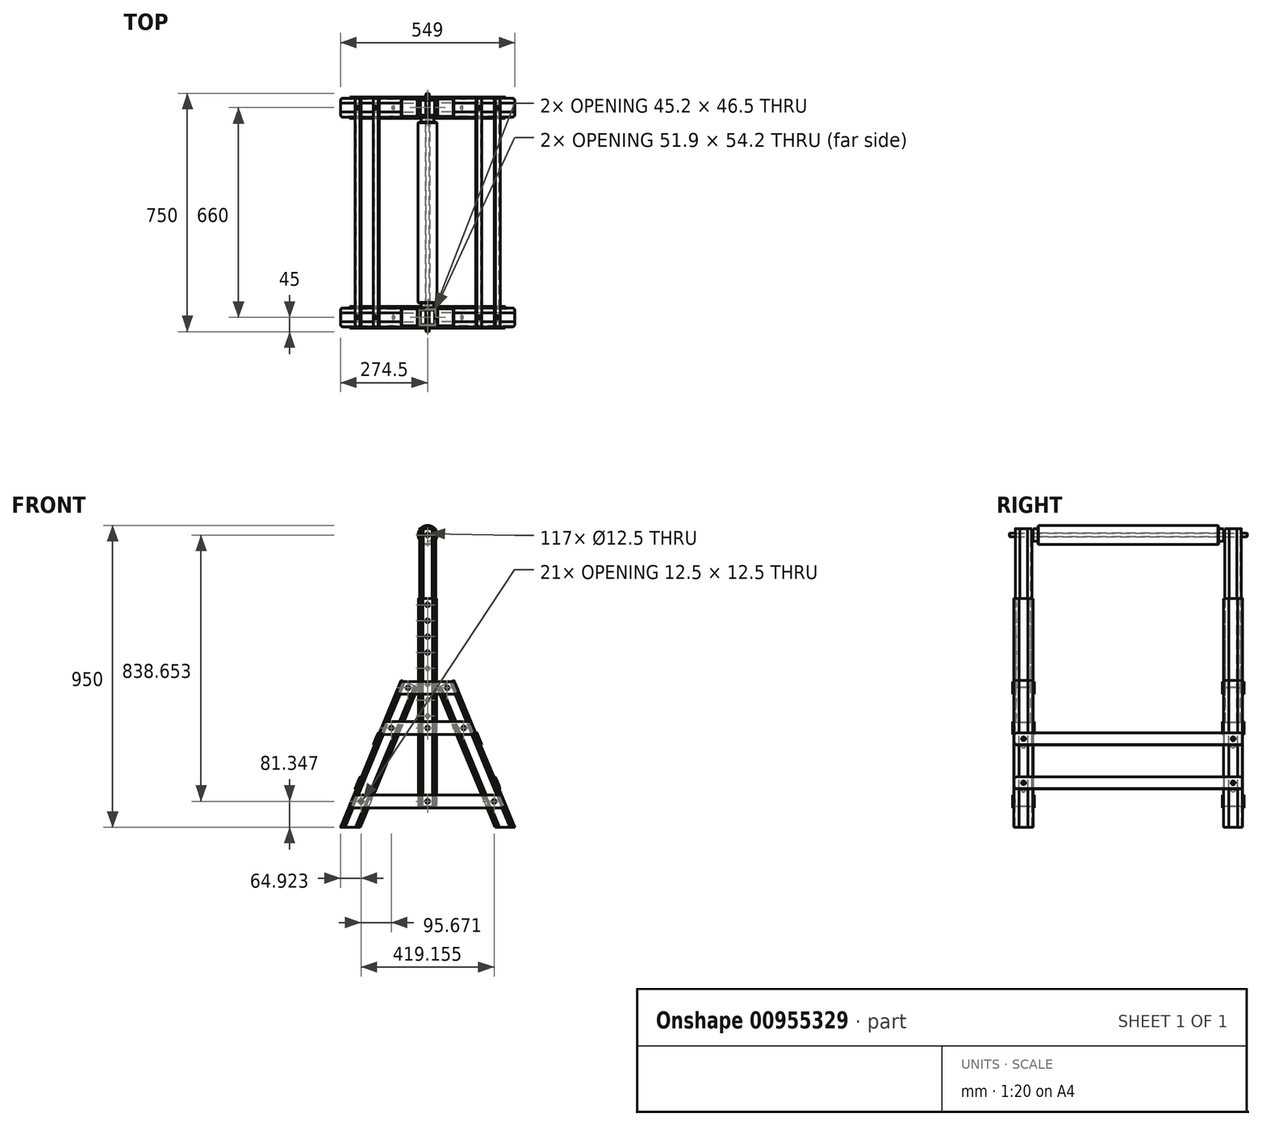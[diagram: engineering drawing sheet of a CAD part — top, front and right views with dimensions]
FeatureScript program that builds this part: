
annotation { "Feature Type Name" : "Feature", "Feature Type Description" : "" }
export const myFeature = defineFeature(function(context is Context, id is Id, definition is map)
    precondition{}
    {
        {
            var Q0;
            Q0=qCreatedBy(makeId("Front.planeOp"),FACE);
            var sketch = newSketch(context, id + "F0", { "sketchPlane" : qUnion([Q0])});
            skLineSegment(sketch, "E0", {"start": v(0, 0) * mm, "end": v(-62.45, 0) * mm});
            skLineSegment(sketch, "E1", {"start": v(-62.45, 0) * mm, "end": v(-244.65, 439.86) * mm});
            skLineSegment(sketch, "E2", {"start": v(-244.65, 439.86) * mm, "end": v(-191.34, 461.94) * mm});
            skLineSegment(sketch, "E3", {"start": v(-191.34, 461.94) * mm, "end": v(0, 0) * mm});
            skLineSegment(sketch, "E4", {"start": v(-218, 450.9) * mm, "end": v(-31.23, 0) * mm, "construction": true});
            skCircle(sketch, "E5", {"center": v(-213.02, 438.89) * mm, "radius": 6.25 * mm});
            skCircle(sketch, "E6", {"center": v(-64.92, 81.35) * mm, "radius": 6.25 * mm});
            skCircle(sketch, "E7", {"center": v(-160.6, 312.32) * mm, "radius": 6.25 * mm});
            skSolve(sketch);
        }
        {
            var Q0;
            Q0=qSketchRegion(id+"F0",true);
            extrude(context, id + "F1", {"entities" : qUnion([Q0]), "depth" : 60 * mm, "offsetDistance" : 25 * mm});
        }
        {
            var Q0;
            Q0=makeQuery(id+"F1.opExtrude","SWEPT_FACE",FACE,{"disambiguationData":[OSD([sQuery(id+"F0.wireOp",EDGE,"E3")])]});
            var sketch = newSketch(context, id + "F2", { "sketchPlane" : qUnion([Q0])});
            skLineSegment(sketch, "E8", {"start": v(-30, 500) * mm, "end": v(-30, 0) * mm, "construction": true});
            skCircle(sketch, "E9", {"center": v(-30, 150) * mm, "radius": 6.25 * mm});
            skCircle(sketch, "E10", {"center": v(-30, 300) * mm, "radius": 6.25 * mm});
            skSolve(sketch);
        }
        {
            var Q0;
            Q0=qSketchRegion(id+"F2",true);
            var Q1;
            Q1=makeQuery(id+"F1.opExtrude","SWEPT_FACE",FACE,{"disambiguationData":[OSD([sQuery(id+"F0.wireOp",EDGE,"E1")])]});
            extrude(context, id + "F3", {"entities" : qUnion([Q0]), "operationType" : NewBodyOperationType.REMOVE, "endBound" : BoundingType.UP_TO_SURFACE, "oppositeDirection" : true, "depth" : 25 * mm, "endBoundEntityFace" : qUnion([Q1]), "offsetDistance" : 25 * mm});
        }
        {
            var Q0;
            Q0=makeQuery(id+"F1.opExtrude","CAP_EDGE",EDGE,{"disambiguationData":[OSD([sQuery(id+"F0.wireOp",EDGE,"E1")])],"isStart":false});
            var Q1;
            Q1=makeQuery(id+"F1.opExtrude","CAP_EDGE",EDGE,{"disambiguationData":[OSD([sQuery(id+"F0.wireOp",EDGE,"E3")])],"isStart":false});
            var Q2;
            Q2=makeQuery(id+"F1.opExtrude","CAP_EDGE",EDGE,{"disambiguationData":[OSD([sQuery(id+"F0.wireOp",EDGE,"E1")])],"isStart":true});
            var Q3;
            Q3=makeQuery(id+"F1.opExtrude","CAP_EDGE",EDGE,{"disambiguationData":[OSD([sQuery(id+"F0.wireOp",EDGE,"E3")])],"isStart":true});
            fillet(context, id + "F4", {"entities" : qUnion([Q0, Q1, Q2, Q3]), "radius" : 7.5 * mm, "tangentPropagation" : true, "allowEdgeOverflow" : false});
        }
        {
            var Q0;
            Q0=makeQuery(id+"F1.opExtrude","SWEPT_FACE",FACE,{"disambiguationData":[OSD([sQuery(id+"F0.wireOp",EDGE,"E2")])]});
            var sketch = newSketch(context, id + "F5", { "sketchPlane" : qUnion([Q0])});
            skLineSegment(sketch, "E11", {"start": v(-57.7, -30) * mm, "end": v(-28.85, -30) * mm, "construction": true});
            skLineSegment(sketch, "E12", {"start": v(-28.85, -30) * mm, "end": v(-28.85, -60) * mm, "construction": true});
            skArc(sketch, "E13.0", {"start": v(-54.8, -52.5) * mm, "mid": v(-53.45, -55.75) * mm, "end": v(-50.2, -57.1) * mm});
            skLineSegment(sketch, "E14", {"start": v(-57.4, -30) * mm, "end": v(-57.4, -44) * mm});
            skLineSegment(sketch, "E15", {"start": v(-57.4, -44) * mm, "end": v(-57.7, -44) * mm});
            skLineSegment(sketch, "E16", {"start": v(-50.2, -60) * mm, "end": v(-49.2, -59) * mm});
            skLineSegment(sketch, "E17", {"start": v(-49.2, -59) * mm, "end": v(-48.2, -60) * mm});
            skLineSegment(sketch, "E18", {"start": v(-48.2, -60) * mm, "end": v(-47.2, -59) * mm});
            skLineSegment(sketch, "E19", {"start": v(-47.2, -59) * mm, "end": v(-46.2, -60) * mm});
            skLineSegment(sketch, "E20", {"start": v(-46.2, -60) * mm, "end": v(-45.2, -59) * mm});
            skLineSegment(sketch, "E21", {"start": v(-45.2, -59) * mm, "end": v(-44.2, -60) * mm});
            skLineSegment(sketch, "E22", {"start": v(-50.2, -57.1) * mm, "end": v(-28.85, -57.1) * mm});
            skLineSegment(sketch, "E23", {"start": v(-54.8, -52.5) * mm, "end": v(-54.8, -30) * mm});
            skLineSegment(sketch, "E24.MirrorCS", {"start": v(-0.3, -44) * mm, "end": v(0, -44) * mm});
            skLineSegment(sketch, "E25.MirrorCS", {"start": v(-12.5, -59) * mm, "end": v(-13.5, -60) * mm});
            skLineSegment(sketch, "E26.MirrorCS", {"start": v(-7.5, -60) * mm, "end": v(-8.5, -59) * mm});
            skLineSegment(sketch, "E27.MirrorCS", {"start": v(-8.5, -59) * mm, "end": v(-9.5, -60) * mm});
            skLineSegment(sketch, "E28.MirrorCS", {"start": v(-11.5, -60) * mm, "end": v(-12.5, -59) * mm});
            skLineSegment(sketch, "E29.MirrorCS", {"start": v(-10.5, -59) * mm, "end": v(-11.5, -60) * mm});
            skLineSegment(sketch, "E30.MirrorCS", {"start": v(-9.5, -60) * mm, "end": v(-10.5, -59) * mm});
            skLineSegment(sketch, "E31.MirrorCS", {"start": v(-0.3, -30) * mm, "end": v(-0.3, -44) * mm});
            skLineSegment(sketch, "E32.MirrorCS", {"start": v(-7.5, -57.1) * mm, "end": v(-28.85, -57.1) * mm});
            skLineSegment(sketch, "E33.MirrorCS", {"start": v(-2.9, -52.5) * mm, "end": v(-2.9, -30) * mm});
            skArc(sketch, "E34.MirrorCS", {"start": v(-2.9, -52.5) * mm, "mid": v(-4.25, -55.75) * mm, "end": v(-7.5, -57.1) * mm});
            skLineSegment(sketch, "E35.MirrorCS", {"start": v(-57.4, -16) * mm, "end": v(-57.7, -16) * mm});
            skLineSegment(sketch, "E36.MirrorCS", {"start": v(-50.2, 0) * mm, "end": v(-49.2, -1) * mm});
            skLineSegment(sketch, "E37.MirrorCS", {"start": v(-45.2, -1) * mm, "end": v(-44.2, 0) * mm});
            skLineSegment(sketch, "E38.MirrorCS", {"start": v(-47.2, -1) * mm, "end": v(-46.2, 0) * mm});
            skLineSegment(sketch, "E39.MirrorCS", {"start": v(-48.2, 0) * mm, "end": v(-47.2, -1) * mm});
            skLineSegment(sketch, "E40.MirrorCS", {"start": v(-49.2, -1) * mm, "end": v(-48.2, 0) * mm});
            skLineSegment(sketch, "E41.MirrorCS", {"start": v(-46.2, 0) * mm, "end": v(-45.2, -1) * mm});
            skLineSegment(sketch, "E42.MirrorCS", {"start": v(-57.4, -30) * mm, "end": v(-57.4, -16) * mm});
            skArc(sketch, "E43.MirrorCS", {"start": v(-54.8, -7.5) * mm, "mid": v(-53.45, -4.25) * mm, "end": v(-50.2, -2.9) * mm});
            skLineSegment(sketch, "E44.MirrorCS", {"start": v(-50.2, -2.9) * mm, "end": v(-28.85, -2.9) * mm});
            skLineSegment(sketch, "E45.MirrorCS", {"start": v(-54.8, -7.5) * mm, "end": v(-54.8, -30) * mm});
            skLineSegment(sketch, "E46.MirrorCS", {"start": v(-0.3, -16) * mm, "end": v(0, -16) * mm});
            skLineSegment(sketch, "E47.MirrorCS", {"start": v(-8.5, -1) * mm, "end": v(-9.5, 0) * mm});
            skLineSegment(sketch, "E48.MirrorCS", {"start": v(-11.5, 0) * mm, "end": v(-12.5, -1) * mm});
            skLineSegment(sketch, "E49.MirrorCS", {"start": v(-10.5, -1) * mm, "end": v(-11.5, 0) * mm});
            skLineSegment(sketch, "E50.MirrorCS", {"start": v(-9.5, 0) * mm, "end": v(-10.5, -1) * mm});
            skLineSegment(sketch, "E51.MirrorCS", {"start": v(-12.5, -1) * mm, "end": v(-13.5, 0) * mm});
            skLineSegment(sketch, "E52.MirrorCS", {"start": v(-7.5, 0) * mm, "end": v(-8.5, -1) * mm});
            skLineSegment(sketch, "E53.MirrorCS", {"start": v(-0.3, -30) * mm, "end": v(-0.3, -16) * mm});
            skLineSegment(sketch, "E54.MirrorCS", {"start": v(-2.9, -7.5) * mm, "end": v(-2.9, -30) * mm});
            skArc(sketch, "E55.MirrorCS", {"start": v(-2.9, -7.5) * mm, "mid": v(-4.25, -4.25) * mm, "end": v(-7.5, -2.9) * mm});
            skLineSegment(sketch, "E56.MirrorCS", {"start": v(-7.5, -2.9) * mm, "end": v(-28.85, -2.9) * mm});
            skSolve(sketch);
        }
        {
            var Q0;
            {var subQ0=sQuery(id+"F5.wireOp",EDGE,"E20");Q0=makeQuery(id+"F5.imprint","IMPRINT",FACE,{"disambiguationData":[TD([[makeQuery(id+"F5.imprint","IMPRINT",EDGE,{"derivedFrom":subQ0}),-1.0]])]});}
            var Q1;
            {var subQ0=sQuery(id+"F5.wireOp",EDGE,"E18");Q1=makeQuery(id+"F5.imprint","IMPRINT",FACE,{"disambiguationData":[TD([[makeQuery(id+"F5.imprint","IMPRINT",EDGE,{"derivedFrom":subQ0}),-1.0]])]});}
            var Q2;
            {var subQ0=sQuery(id+"F5.wireOp",EDGE,"E16");Q2=makeQuery(id+"F5.imprint","IMPRINT",FACE,{"disambiguationData":[TD([[makeQuery(id+"F5.imprint","IMPRINT",EDGE,{"derivedFrom":subQ0}),-1.0]])]});}
            var Q3;
            {var subQ0=sQuery(id+"F5.wireOp",EDGE,"E26.MirrorCS");Q3=makeQuery(id+"F5.imprint","IMPRINT",FACE,{"disambiguationData":[TD([[makeQuery(id+"F5.imprint","IMPRINT",EDGE,{"derivedFrom":subQ0}),1.0]])]});}
            var Q4;
            {var subQ0=sQuery(id+"F5.wireOp",EDGE,"E29.MirrorCS");Q4=makeQuery(id+"F5.imprint","IMPRINT",FACE,{"disambiguationData":[TD([[makeQuery(id+"F5.imprint","IMPRINT",EDGE,{"derivedFrom":subQ0}),1.0]])]});}
            var Q5;
            {var subQ0=sQuery(id+"F5.wireOp",EDGE,"E25.MirrorCS");Q5=makeQuery(id+"F5.imprint","IMPRINT",FACE,{"disambiguationData":[TD([[makeQuery(id+"F5.imprint","IMPRINT",EDGE,{"derivedFrom":subQ0}),1.0]])]});}
            var Q6;
            {var subQ1=sQuery(id+"F5.wireOp",EDGE,"E24.MirrorCS");Q6=makeQuery(id+"F5.imprint","IMPRINT",FACE,{"disambiguationData":[TD([[makeQuery(id+"F5.imprint","IMPRINT",EDGE,{"derivedFrom":subQ1}),1.0]])]});}
            var Q7;
            Q7=makeQuery(id+"F5.imprint","IMPRINT",FACE,{"disambiguationData":[TD([[makeQuery(id+"F5.imprint","IMPRINT",EDGE,{"derivedFrom":sQuery(id+"F5.wireOp",EDGE,"E14")}),-1.0]])]});
            var Q8;
            {var subQ0=sQuery(id+"F5.wireOp",EDGE,"E36.MirrorCS");Q8=makeQuery(id+"F5.imprint","IMPRINT",FACE,{"disambiguationData":[TD([[makeQuery(id+"F5.imprint","IMPRINT",EDGE,{"derivedFrom":subQ0}),1.0]])]});}
            var Q9;
            {var subQ0=sQuery(id+"F5.wireOp",EDGE,"E38.MirrorCS");Q9=makeQuery(id+"F5.imprint","IMPRINT",FACE,{"disambiguationData":[TD([[makeQuery(id+"F5.imprint","IMPRINT",EDGE,{"derivedFrom":subQ0}),1.0]])]});}
            var Q10;
            {var subQ0=sQuery(id+"F5.wireOp",EDGE,"E37.MirrorCS");Q10=makeQuery(id+"F5.imprint","IMPRINT",FACE,{"disambiguationData":[TD([[makeQuery(id+"F5.imprint","IMPRINT",EDGE,{"derivedFrom":subQ0}),1.0]])]});}
            var Q11;
            {var subQ0=sQuery(id+"F5.wireOp",EDGE,"E47.MirrorCS");Q11=makeQuery(id+"F5.imprint","IMPRINT",FACE,{"disambiguationData":[TD([[makeQuery(id+"F5.imprint","IMPRINT",EDGE,{"derivedFrom":subQ0}),-1.0]])]});}
            var Q12;
            {var subQ0=sQuery(id+"F5.wireOp",EDGE,"E49.MirrorCS");Q12=makeQuery(id+"F5.imprint","IMPRINT",FACE,{"disambiguationData":[TD([[makeQuery(id+"F5.imprint","IMPRINT",EDGE,{"derivedFrom":subQ0}),-1.0]])]});}
            var Q13;
            {var subQ0=sQuery(id+"F5.wireOp",EDGE,"E48.MirrorCS");Q13=makeQuery(id+"F5.imprint","IMPRINT",FACE,{"disambiguationData":[TD([[makeQuery(id+"F5.imprint","IMPRINT",EDGE,{"derivedFrom":subQ0}),-1.0]])]});}
            var Q14;
            Q14=makeQuery(id+"F5.imprint","IMPRINT",FACE,{"disambiguationData":[TD([[makeQuery(id+"F5.imprint","IMPRINT",EDGE,{"derivedFrom":sQuery(id+"F5.wireOp",EDGE,"E13.0")}),1.0]])]});
            var Q15;
            Q15=makeQuery(id+"F1.opExtrude","SWEPT_FACE",FACE,{"disambiguationData":[OSD([sQuery(id+"F0.wireOp",EDGE,"E0")])]});
            extrude(context, id + "F6", {"entities" : qUnion([Q0, Q1, Q2, Q3, Q4, Q5, Q6, Q7, Q8, Q9, Q10, Q11, Q12, Q13, Q14]), "operationType" : NewBodyOperationType.REMOVE, "endBound" : BoundingType.UP_TO_SURFACE, "oppositeDirection" : true, "depth" : 25 * mm, "endBoundEntityFace" : qUnion([Q15]), "offsetDistance" : 25 * mm});
        }
        {
            var Q0;
            Q0=makeQuery(id+"F1.opExtrude","CAP_FACE",FACE,{"disambiguationData":[OSD([sQuery(id+"F0.wireOp",EDGE,"E0"),sQuery(id+"F0.wireOp",EDGE,"E1"),sQuery(id+"F0.wireOp",EDGE,"E2"),sQuery(id+"F0.wireOp",EDGE,"E3"),sQuery(id+"F0.wireOp",EDGE,"E5"),sQuery(id+"F0.wireOp",EDGE,"E6")])],"isStart":false});
            var sketch = newSketch(context, id + "F7", { "sketchPlane" : qUnion([Q0])});
            skLineSegment(sketch, "E57", {"start": v(-245.65, 720) * mm, "end": v(-245.65, 66.35) * mm});
            skLineSegment(sketch, "E58", {"start": v(-245.65, 66.35) * mm, "end": v(-303.35, 66.35) * mm});
            skLineSegment(sketch, "E59", {"start": v(-303.35, 66.35) * mm, "end": v(-303.35, 720) * mm});
            skLineSegment(sketch, "E60", {"start": v(-303.35, 720) * mm, "end": v(-245.65, 720) * mm});
            skLineSegment(sketch, "E61", {"start": v(-303.35, 75.1) * mm, "end": v(24.53, 75.1) * mm, "construction": true});
            skLineSegment(sketch, "E62", {"start": v(-274.5, 720) * mm, "end": v(-274.5, 66.35) * mm, "construction": true});
            skCircle(sketch, "E63", {"center": v(-274.5, 81.35) * mm, "radius": 6.25 * mm});
            skLineSegment(sketch, "E64", {"start": v(-303.35, 306.07) * mm, "end": v(155.56, 306.07) * mm, "construction": true});
            skCircle(sketch, "E65", {"center": v(-274.5, 312.32) * mm, "radius": 6.25 * mm});
            skCircle(sketch, "E66", {"center": v(-274.5, 650) * mm, "radius": 6.25 * mm});
            skCircle(sketch, "E67", {"center": v(-274.5, 600) * mm, "radius": 6.25 * mm});
            skCircle(sketch, "E68", {"center": v(-274.5, 700) * mm, "radius": 6.25 * mm});
            skCircle(sketch, "E69", {"center": v(-274.5, 550) * mm, "radius": 6.25 * mm});
            skSolve(sketch);
        }
        {
            var Q0;
            Q0=qSketchRegion(id+"F7",true);
            extrude(context, id + "F8", {"entities" : qUnion([Q0]), "oppositeDirection" : true, "depth" : 60 * mm, "offsetDistance" : 25 * mm});
        }
        {
            var Q0;
            Q0=makeQuery(id+"F8.opExtrude","CAP_EDGE",EDGE,{"disambiguationData":[OSD([sQuery(id+"F7.wireOp",EDGE,"E59")])],"isStart":false});
            var Q1;
            Q1=makeQuery(id+"F8.opExtrude","CAP_EDGE",EDGE,{"disambiguationData":[OSD([sQuery(id+"F7.wireOp",EDGE,"E59")])],"isStart":true});
            var Q2;
            Q2=makeQuery(id+"F8.opExtrude","CAP_EDGE",EDGE,{"disambiguationData":[OSD([sQuery(id+"F7.wireOp",EDGE,"E57")])],"isStart":true});
            var Q3;
            Q3=makeQuery(id+"F8.opExtrude","CAP_EDGE",EDGE,{"disambiguationData":[OSD([sQuery(id+"F7.wireOp",EDGE,"E57")])],"isStart":false});
            fillet(context, id + "F9", {"entities" : qUnion([Q0, Q1, Q2, Q3]), "radius" : 7.5 * mm, "tangentPropagation" : true, "allowEdgeOverflow" : false});
        }
        {
            var Q0;
            Q0=makeQuery(id+"F8.opExtrude","SWEPT_FACE",FACE,{"disambiguationData":[OSD([sQuery(id+"F7.wireOp",EDGE,"E60")])]});
            var sketch = newSketch(context, id + "F10", { "sketchPlane" : qUnion([Q0])});
            skLineSegment(sketch, "E70", {"start": v(-274.5, -60) * mm, "end": v(-274.5, -30) * mm, "construction": true});
            skPoint(sketch, "E70.endSnap0", {"position": v(-303.35, -30) * mm});
            skLineSegment(sketch, "E71", {"start": v(-274.5, -30) * mm, "end": v(-303.35, -30) * mm, "construction": true});
            skLineSegment(sketch, "E72", {"start": v(-295.85, -60) * mm, "end": v(-294.85, -59) * mm});
            skLineSegment(sketch, "E73", {"start": v(-294.85, -59) * mm, "end": v(-293.85, -60) * mm});
            skLineSegment(sketch, "E74", {"start": v(-293.85, -60) * mm, "end": v(-292.85, -59) * mm});
            skLineSegment(sketch, "E75", {"start": v(-292.85, -59) * mm, "end": v(-291.85, -60) * mm});
            skLineSegment(sketch, "E76", {"start": v(-291.85, -60) * mm, "end": v(-290.85, -59) * mm});
            skLineSegment(sketch, "E77", {"start": v(-290.85, -59) * mm, "end": v(-289.85, -60) * mm});
            skLineSegment(sketch, "E78", {"start": v(-303.05, -30) * mm, "end": v(-303.05, -44) * mm});
            skLineSegment(sketch, "E79", {"start": v(-303.05, -44) * mm, "end": v(-303.35, -44) * mm});
            skArc(sketch, "E80.0", {"start": v(-300.45, -52.5) * mm, "mid": v(-299.1, -55.75) * mm, "end": v(-295.85, -57.1) * mm});
            skLineSegment(sketch, "E81", {"start": v(-295.85, -57.1) * mm, "end": v(-274.5, -57.1) * mm});
            skLineSegment(sketch, "E82", {"start": v(-300.45, -52.5) * mm, "end": v(-300.45, -30) * mm});
            skLineSegment(sketch, "E83.MirrorCS", {"start": v(-255.15, -60) * mm, "end": v(-256.15, -59) * mm});
            skLineSegment(sketch, "E84.MirrorCS", {"start": v(-245.95, -44) * mm, "end": v(-245.65, -44) * mm});
            skLineSegment(sketch, "E85.MirrorCS", {"start": v(-254.15, -59) * mm, "end": v(-255.15, -60) * mm});
            skLineSegment(sketch, "E86.MirrorCS", {"start": v(-256.15, -59) * mm, "end": v(-257.15, -60) * mm});
            skLineSegment(sketch, "E87.MirrorCS", {"start": v(-257.15, -60) * mm, "end": v(-258.15, -59) * mm});
            skLineSegment(sketch, "E88.MirrorCS", {"start": v(-253.15, -60) * mm, "end": v(-254.15, -59) * mm});
            skLineSegment(sketch, "E89.MirrorCS", {"start": v(-258.15, -59) * mm, "end": v(-259.15, -60) * mm});
            skLineSegment(sketch, "E90.MirrorCS", {"start": v(-248.55, -52.5) * mm, "end": v(-248.55, -30) * mm});
            skLineSegment(sketch, "E91.MirrorCS", {"start": v(-245.95, -30) * mm, "end": v(-245.95, -44) * mm});
            skLineSegment(sketch, "E92.MirrorCS", {"start": v(-253.15, -57.1) * mm, "end": v(-274.5, -57.1) * mm});
            skArc(sketch, "E93.MirrorCS", {"start": v(-248.55, -52.5) * mm, "mid": v(-249.9, -55.75) * mm, "end": v(-253.15, -57.1) * mm});
            skLineSegment(sketch, "E94.MirrorCS", {"start": v(-290.85, -1) * mm, "end": v(-289.85, 0) * mm});
            skLineSegment(sketch, "E95.MirrorCS", {"start": v(-303.05, -16) * mm, "end": v(-303.35, -16) * mm});
            skLineSegment(sketch, "E96.MirrorCS", {"start": v(-295.85, 0) * mm, "end": v(-294.85, -1) * mm});
            skLineSegment(sketch, "E97.MirrorCS", {"start": v(-293.85, 0) * mm, "end": v(-292.85, -1) * mm});
            skLineSegment(sketch, "E98.MirrorCS", {"start": v(-294.85, -1) * mm, "end": v(-293.85, 0) * mm});
            skLineSegment(sketch, "E99.MirrorCS", {"start": v(-291.85, 0) * mm, "end": v(-290.85, -1) * mm});
            skLineSegment(sketch, "E100.MirrorCS", {"start": v(-292.85, -1) * mm, "end": v(-291.85, 0) * mm});
            skLineSegment(sketch, "E101.MirrorCS", {"start": v(-300.45, -7.5) * mm, "end": v(-300.45, -30) * mm});
            skLineSegment(sketch, "E102.MirrorCS", {"start": v(-295.85, -2.9) * mm, "end": v(-274.5, -2.9) * mm});
            skArc(sketch, "E103.MirrorCS", {"start": v(-300.45, -7.5) * mm, "mid": v(-299.1, -4.25) * mm, "end": v(-295.85, -2.9) * mm});
            skLineSegment(sketch, "E104.MirrorCS", {"start": v(-303.05, -30) * mm, "end": v(-303.05, -16) * mm});
            skLineSegment(sketch, "E105.MirrorCS", {"start": v(-253.15, 0) * mm, "end": v(-254.15, -1) * mm});
            skLineSegment(sketch, "E106.MirrorCS", {"start": v(-258.15, -1) * mm, "end": v(-259.15, 0) * mm});
            skLineSegment(sketch, "E107.MirrorCS", {"start": v(-255.15, 0) * mm, "end": v(-256.15, -1) * mm});
            skLineSegment(sketch, "E108.MirrorCS", {"start": v(-257.15, 0) * mm, "end": v(-258.15, -1) * mm});
            skLineSegment(sketch, "E109.MirrorCS", {"start": v(-256.15, -1) * mm, "end": v(-257.15, 0) * mm});
            skLineSegment(sketch, "E110.MirrorCS", {"start": v(-245.95, -16) * mm, "end": v(-245.65, -16) * mm});
            skLineSegment(sketch, "E111.MirrorCS", {"start": v(-254.15, -1) * mm, "end": v(-255.15, 0) * mm});
            skLineSegment(sketch, "E112.MirrorCS", {"start": v(-248.55, -7.5) * mm, "end": v(-248.55, -30) * mm});
            skLineSegment(sketch, "E113.MirrorCS", {"start": v(-245.95, -30) * mm, "end": v(-245.95, -16) * mm});
            skArc(sketch, "E114.MirrorCS", {"start": v(-248.55, -7.5) * mm, "mid": v(-249.9, -4.25) * mm, "end": v(-253.15, -2.9) * mm});
            skLineSegment(sketch, "E115.MirrorCS", {"start": v(-253.15, -2.9) * mm, "end": v(-274.5, -2.9) * mm});
            skSolve(sketch);
        }
        {
            var Q0;
            {var subQ0=sQuery(id+"F10.wireOp",EDGE,"E76");Q0=makeQuery(id+"F10.imprint","IMPRINT",FACE,{"disambiguationData":[TD([[makeQuery(id+"F10.imprint","IMPRINT",EDGE,{"derivedFrom":subQ0}),-1.0]])]});}
            var Q1;
            {var subQ0=sQuery(id+"F10.wireOp",EDGE,"E74");Q1=makeQuery(id+"F10.imprint","IMPRINT",FACE,{"disambiguationData":[TD([[makeQuery(id+"F10.imprint","IMPRINT",EDGE,{"derivedFrom":subQ0}),-1.0]])]});}
            var Q2;
            {var subQ0=sQuery(id+"F10.wireOp",EDGE,"E72");Q2=makeQuery(id+"F10.imprint","IMPRINT",FACE,{"disambiguationData":[TD([[makeQuery(id+"F10.imprint","IMPRINT",EDGE,{"derivedFrom":subQ0}),-1.0]])]});}
            var Q3;
            Q3=makeQuery(id+"F10.imprint","IMPRINT",FACE,{"disambiguationData":[TD([[makeQuery(id+"F10.imprint","IMPRINT",EDGE,{"derivedFrom":sQuery(id+"F10.wireOp",EDGE,"E78")}),-1.0]])]});
            var Q4;
            {var subQ0=sQuery(id+"F10.wireOp",EDGE,"E85.MirrorCS");Q4=makeQuery(id+"F10.imprint","IMPRINT",FACE,{"disambiguationData":[TD([[makeQuery(id+"F10.imprint","IMPRINT",EDGE,{"derivedFrom":subQ0}),1.0]])]});}
            var Q5;
            {var subQ0=sQuery(id+"F10.wireOp",EDGE,"E83.MirrorCS");Q5=makeQuery(id+"F10.imprint","IMPRINT",FACE,{"disambiguationData":[TD([[makeQuery(id+"F10.imprint","IMPRINT",EDGE,{"derivedFrom":subQ0}),1.0]])]});}
            var Q6;
            {var subQ0=sQuery(id+"F10.wireOp",EDGE,"E87.MirrorCS");Q6=makeQuery(id+"F10.imprint","IMPRINT",FACE,{"disambiguationData":[TD([[makeQuery(id+"F10.imprint","IMPRINT",EDGE,{"derivedFrom":subQ0}),1.0]])]});}
            var Q7;
            {var subQ1=sQuery(id+"F10.wireOp",EDGE,"E84.MirrorCS");Q7=makeQuery(id+"F10.imprint","IMPRINT",FACE,{"disambiguationData":[TD([[makeQuery(id+"F10.imprint","IMPRINT",EDGE,{"derivedFrom":subQ1}),1.0]])]});}
            var Q8;
            {var subQ0=sQuery(id+"F10.wireOp",EDGE,"E105.MirrorCS");Q8=makeQuery(id+"F10.imprint","IMPRINT",FACE,{"disambiguationData":[TD([[makeQuery(id+"F10.imprint","IMPRINT",EDGE,{"derivedFrom":subQ0}),-1.0]])]});}
            var Q9;
            {var subQ0=sQuery(id+"F10.wireOp",EDGE,"E107.MirrorCS");Q9=makeQuery(id+"F10.imprint","IMPRINT",FACE,{"disambiguationData":[TD([[makeQuery(id+"F10.imprint","IMPRINT",EDGE,{"derivedFrom":subQ0}),-1.0]])]});}
            var Q10;
            {var subQ0=sQuery(id+"F10.wireOp",EDGE,"E106.MirrorCS");Q10=makeQuery(id+"F10.imprint","IMPRINT",FACE,{"disambiguationData":[TD([[makeQuery(id+"F10.imprint","IMPRINT",EDGE,{"derivedFrom":subQ0}),-1.0]])]});}
            var Q11;
            {var subQ0=sQuery(id+"F10.wireOp",EDGE,"E96.MirrorCS");Q11=makeQuery(id+"F10.imprint","IMPRINT",FACE,{"disambiguationData":[TD([[makeQuery(id+"F10.imprint","IMPRINT",EDGE,{"derivedFrom":subQ0}),1.0]])]});}
            var Q12;
            {var subQ0=sQuery(id+"F10.wireOp",EDGE,"E97.MirrorCS");Q12=makeQuery(id+"F10.imprint","IMPRINT",FACE,{"disambiguationData":[TD([[makeQuery(id+"F10.imprint","IMPRINT",EDGE,{"derivedFrom":subQ0}),1.0]])]});}
            var Q13;
            {var subQ0=sQuery(id+"F10.wireOp",EDGE,"E94.MirrorCS");Q13=makeQuery(id+"F10.imprint","IMPRINT",FACE,{"disambiguationData":[TD([[makeQuery(id+"F10.imprint","IMPRINT",EDGE,{"derivedFrom":subQ0}),1.0]])]});}
            var Q14;
            Q14=makeQuery(id+"F10.imprint","IMPRINT",FACE,{"disambiguationData":[TD([[makeQuery(id+"F10.imprint","IMPRINT",EDGE,{"derivedFrom":sQuery(id+"F10.wireOp",EDGE,"E80.0")}),1.0]])]});
            var Q15;
            Q15=makeQuery(id+"F8.opExtrude","SWEPT_FACE",FACE,{"disambiguationData":[OSD([sQuery(id+"F7.wireOp",EDGE,"E58")])]});
            extrude(context, id + "F11", {"entities" : qUnion([Q0, Q1, Q2, Q3, Q4, Q5, Q6, Q7, Q8, Q9, Q10, Q11, Q12, Q13, Q14]), "operationType" : NewBodyOperationType.REMOVE, "endBound" : BoundingType.UP_TO_SURFACE, "oppositeDirection" : true, "depth" : 25 * mm, "endBoundEntityFace" : qUnion([Q15]), "offsetDistance" : 25 * mm});
        }
        {
            var Q0;
            Q0=makeQuery(id+"F11.boolean.opBoolean","COPY",FACE,{"derivedFrom":makeQuery(id+"F11.opExtrude","SWEPT_FACE",FACE,{"disambiguationData":[OSD([sQuery(id+"F10.wireOp",EDGE,"E82"),sQuery(id+"F10.wireOp",EDGE,"E101.MirrorCS")])]})});
            var Q1;
            Q1=makeQuery(id+"F11.boolean.opBoolean","COPY",FACE,{"derivedFrom":makeQuery(id+"F11.opExtrude","SWEPT_FACE",FACE,{"disambiguationData":[OSD([sQuery(id+"F10.wireOp",EDGE,"E90.MirrorCS"),sQuery(id+"F10.wireOp",EDGE,"E112.MirrorCS")])]})});
            cPlane(context, id + "F12", {"entities" : qUnion([Q0, Q1]), "cplaneType" : CPlaneType.MID_PLANE, "offset" : 25 * mm, "width" : 150 * mm, "height" : 150 * mm});
        }
        {
            var Q0;
            Q0=makeQuery(id+"F11.boolean.opBoolean","COPY",FACE,{"derivedFrom":makeQuery(id+"F11.opExtrude","SWEPT_FACE",FACE,{"disambiguationData":[OSD([sQuery(id+"F10.wireOp",EDGE,"E81"),sQuery(id+"F10.wireOp",EDGE,"E92.MirrorCS")])]})});
            var Q1;
            Q1=makeQuery(id+"F11.boolean.opBoolean","COPY",FACE,{"derivedFrom":makeQuery(id+"F11.opExtrude","SWEPT_FACE",FACE,{"disambiguationData":[OSD([sQuery(id+"F10.wireOp",EDGE,"E102.MirrorCS"),sQuery(id+"F10.wireOp",EDGE,"E115.MirrorCS")])]})});
            cPlane(context, id + "F13", {"entities" : qUnion([Q0, Q1]), "cplaneType" : CPlaneType.MID_PLANE, "offset" : 25 * mm, "width" : 150 * mm, "height" : 150 * mm});
        }
        {
            var Q0;
            Q0=makeQuery(id+"F8.opExtrude","CAP_EDGE",EDGE,{"disambiguationData":[OSD([sQuery(id+"F7.wireOp",EDGE,"E65")])],"isStart":false});
            cPlane(context, id + "F14", {"entities" : qUnion([Q0]), "cplaneType" : CPlaneType.LINE_ANGLE, "offset" : 25 * mm, "angle" : 0 * degree, "width" : 150 * mm, "height" : 150 * mm});
        }
        {
            var Q0;
            Q0=qCreatedBy(id+"F13.planeOp",FACE);
            var sketch = newSketch(context, id + "F15", { "sketchPlane" : qUnion([Q0])});
            skLineSegment(sketch, "E116", {"start": v(249, 940) * mm, "end": v(249, 330) * mm});
            skLineSegment(sketch, "E117", {"start": v(249, 330) * mm, "end": v(300, 330) * mm});
            skLineSegment(sketch, "E118", {"start": v(300, 330) * mm, "end": v(300, 940) * mm});
            skLineSegment(sketch, "E119", {"start": v(300, 940) * mm, "end": v(249, 940) * mm});
            skLineSegment(sketch, "E120", {"start": v(274.5, 940) * mm, "end": v(274.5, 330) * mm, "construction": true});
            skCircle(sketch, "E121", {"center": v(274.5, 550) * mm, "radius": 6.25 * mm});
            skCircle(sketch, "E122", {"center": v(274.5, 500) * mm, "radius": 6.25 * mm});
            skCircle(sketch, "E123", {"center": v(274.5, 650) * mm, "radius": 6.25 * mm});
            skCircle(sketch, "E124", {"center": v(274.5, 450) * mm, "radius": 6.25 * mm});
            skCircle(sketch, "E125", {"center": v(274.5, 700) * mm, "radius": 6.25 * mm});
            skCircle(sketch, "E126", {"center": v(274.5, 600) * mm, "radius": 6.25 * mm});
            skCircle(sketch, "E127", {"center": v(274.5, 400) * mm, "radius": 6.25 * mm});
            skCircle(sketch, "E128", {"center": v(274.5, 350) * mm, "radius": 6.25 * mm});
            skCircle(sketch, "E129", {"center": v(274.5, 920) * mm, "radius": 6.25 * mm});
            skSolve(sketch);
        }
        {
            var Q0;
            Q0=qSketchRegion(id+"F15",true);
            extrude(context, id + "F16", {"entities" : qUnion([Q0]), "endBound" : BoundingType.SYMMETRIC, "depth" : 52.3 * mm, "offsetDistance" : 25 * mm});
        }
        {
            var Q0;
            Q0=makeQuery(id+"F16.opExtrude","CAP_EDGE",EDGE,{"disambiguationData":[OSD([sQuery(id+"F15.wireOp",EDGE,"E116")])],"isStart":true});
            var Q1;
            Q1=makeQuery(id+"F16.opExtrude","CAP_EDGE",EDGE,{"disambiguationData":[OSD([sQuery(id+"F15.wireOp",EDGE,"E118")])],"isStart":true});
            var Q2;
            Q2=makeQuery(id+"F16.opExtrude","CAP_EDGE",EDGE,{"disambiguationData":[OSD([sQuery(id+"F15.wireOp",EDGE,"E116")])],"isStart":false});
            var Q3;
            Q3=makeQuery(id+"F16.opExtrude","CAP_EDGE",EDGE,{"disambiguationData":[OSD([sQuery(id+"F15.wireOp",EDGE,"E118")])],"isStart":false});
            fillet(context, id + "F17", {"entities" : qUnion([Q0, Q1, Q2, Q3]), "radius" : 7.5 * mm, "tangentPropagation" : true, "allowEdgeOverflow" : false});
        }
        {
            var Q0;
            Q0=makeQuery(id+"F16.opExtrude","SWEPT_FACE",FACE,{"disambiguationData":[OSD([sQuery(id+"F15.wireOp",EDGE,"E119")])]});
            var sketch = newSketch(context, id + "F18", { "sketchPlane" : qUnion([Q0])});
            skLineSegment(sketch, "E130", {"start": v(-249, -30) * mm, "end": v(-274.5, -30) * mm, "construction": true});
            skPoint(sketch, "E130.endSnap0", {"position": v(-274.5, -3.85) * mm});
            skLineSegment(sketch, "E131", {"start": v(-274.5, -30) * mm, "end": v(-274.5, -3.85) * mm, "construction": true});
            skLineSegment(sketch, "E132", {"start": v(-256.5, -3.85) * mm, "end": v(-257.5, -4.85) * mm});
            skLineSegment(sketch, "E133", {"start": v(-257.5, -4.85) * mm, "end": v(-258.5, -3.85) * mm});
            skLineSegment(sketch, "E134", {"start": v(-258.5, -3.85) * mm, "end": v(-259.5, -4.85) * mm});
            skLineSegment(sketch, "E135", {"start": v(-259.5, -4.85) * mm, "end": v(-260.5, -3.85) * mm});
            skLineSegment(sketch, "E136", {"start": v(-249.25, -30) * mm, "end": v(-249.25, -17.85) * mm});
            skLineSegment(sketch, "E137", {"start": v(-249.25, -17.85) * mm, "end": v(-249, -17.85) * mm});
            skArc(sketch, "E138.0", {"start": v(-251.9, -11.35) * mm, "mid": v(-253.25, -8.1) * mm, "end": v(-256.5, -6.75) * mm});
            skLineSegment(sketch, "E139", {"start": v(-256.5, -6.75) * mm, "end": v(-274.5, -6.75) * mm});
            skLineSegment(sketch, "E140", {"start": v(-251.9, -11.35) * mm, "end": v(-251.9, -30) * mm});
            skLineSegment(sketch, "E141.MirrorCS", {"start": v(-299.75, -17.85) * mm, "end": v(-300, -17.85) * mm});
            skLineSegment(sketch, "E142.MirrorCS", {"start": v(-292.5, -3.85) * mm, "end": v(-291.5, -4.85) * mm});
            skLineSegment(sketch, "E143.MirrorCS", {"start": v(-290.5, -3.85) * mm, "end": v(-289.5, -4.85) * mm});
            skLineSegment(sketch, "E144.MirrorCS", {"start": v(-289.5, -4.85) * mm, "end": v(-288.5, -3.85) * mm});
            skLineSegment(sketch, "E145.MirrorCS", {"start": v(-291.5, -4.85) * mm, "end": v(-290.5, -3.85) * mm});
            skLineSegment(sketch, "E146.MirrorCS", {"start": v(-299.75, -30) * mm, "end": v(-299.75, -17.85) * mm});
            skLineSegment(sketch, "E147.MirrorCS", {"start": v(-297.1, -11.35) * mm, "end": v(-297.1, -30) * mm});
            skLineSegment(sketch, "E148.MirrorCS", {"start": v(-292.5, -6.75) * mm, "end": v(-274.5, -6.75) * mm});
            skArc(sketch, "E149.MirrorCS", {"start": v(-297.1, -11.35) * mm, "mid": v(-295.75, -8.1) * mm, "end": v(-292.5, -6.75) * mm});
            skLineSegment(sketch, "E150.MirrorCS", {"start": v(-258.5, -56.15) * mm, "end": v(-259.5, -55.15) * mm});
            skLineSegment(sketch, "E151.MirrorCS", {"start": v(-249.25, -42.15) * mm, "end": v(-249, -42.15) * mm});
            skLineSegment(sketch, "E152.MirrorCS", {"start": v(-257.5, -55.15) * mm, "end": v(-258.5, -56.15) * mm});
            skLineSegment(sketch, "E153.MirrorCS", {"start": v(-256.5, -56.15) * mm, "end": v(-257.5, -55.15) * mm});
            skLineSegment(sketch, "E154.MirrorCS", {"start": v(-259.5, -55.15) * mm, "end": v(-260.5, -56.15) * mm});
            skLineSegment(sketch, "E155.MirrorCS", {"start": v(-256.5, -53.25) * mm, "end": v(-274.5, -53.25) * mm});
            skArc(sketch, "E156.MirrorCS", {"start": v(-251.9, -48.65) * mm, "mid": v(-253.25, -51.9) * mm, "end": v(-256.5, -53.25) * mm});
            skLineSegment(sketch, "E157.MirrorCS", {"start": v(-249.25, -30) * mm, "end": v(-249.25, -42.15) * mm});
            skLineSegment(sketch, "E158.MirrorCS", {"start": v(-251.9, -48.65) * mm, "end": v(-251.9, -30) * mm});
            skLineSegment(sketch, "E159.MirrorCS", {"start": v(-299.75, -42.15) * mm, "end": v(-300, -42.15) * mm});
            skLineSegment(sketch, "E160.MirrorCS", {"start": v(-291.5, -55.15) * mm, "end": v(-290.5, -56.15) * mm});
            skLineSegment(sketch, "E161.MirrorCS", {"start": v(-290.5, -56.15) * mm, "end": v(-289.5, -55.15) * mm});
            skLineSegment(sketch, "E162.MirrorCS", {"start": v(-292.5, -56.15) * mm, "end": v(-291.5, -55.15) * mm});
            skLineSegment(sketch, "E163.MirrorCS", {"start": v(-289.5, -55.15) * mm, "end": v(-288.5, -56.15) * mm});
            skLineSegment(sketch, "E164.MirrorCS", {"start": v(-299.75, -30) * mm, "end": v(-299.75, -42.15) * mm});
            skArc(sketch, "E165.MirrorCS", {"start": v(-297.1, -48.65) * mm, "mid": v(-295.75, -51.9) * mm, "end": v(-292.5, -53.25) * mm});
            skLineSegment(sketch, "E166.MirrorCS", {"start": v(-297.1, -48.65) * mm, "end": v(-297.1, -30) * mm});
            skLineSegment(sketch, "E167.MirrorCS", {"start": v(-292.5, -53.25) * mm, "end": v(-274.5, -53.25) * mm});
            skSolve(sketch);
        }
        {
            var Q0;
            Q0=makeQuery(id+"F18.imprint","IMPRINT",FACE,{"disambiguationData":[TD([[makeQuery(id+"F18.imprint","IMPRINT",EDGE,{"derivedFrom":sQuery(id+"F18.wireOp",EDGE,"E136")}),-1.0]])]});
            var Q1;
            {var subQ1=sQuery(id+"F18.wireOp",EDGE,"E141.MirrorCS");Q1=makeQuery(id+"F18.imprint","IMPRINT",FACE,{"disambiguationData":[TD([[makeQuery(id+"F18.imprint","IMPRINT",EDGE,{"derivedFrom":subQ1}),1.0]])]});}
            var Q2;
            {var subQ0=sQuery(id+"F18.wireOp",EDGE,"E160.MirrorCS");Q2=makeQuery(id+"F18.imprint","IMPRINT",FACE,{"disambiguationData":[TD([[makeQuery(id+"F18.imprint","IMPRINT",EDGE,{"derivedFrom":subQ0}),-1.0]])]});}
            var Q3;
            {var subQ0=sQuery(id+"F18.wireOp",EDGE,"E161.MirrorCS");Q3=makeQuery(id+"F18.imprint","IMPRINT",FACE,{"disambiguationData":[TD([[makeQuery(id+"F18.imprint","IMPRINT",EDGE,{"derivedFrom":subQ0}),-1.0]])]});}
            var Q4;
            {var subQ0=sQuery(id+"F18.wireOp",EDGE,"E152.MirrorCS");Q4=makeQuery(id+"F18.imprint","IMPRINT",FACE,{"disambiguationData":[TD([[makeQuery(id+"F18.imprint","IMPRINT",EDGE,{"derivedFrom":subQ0}),1.0]])]});}
            var Q5;
            {var subQ0=sQuery(id+"F18.wireOp",EDGE,"E150.MirrorCS");Q5=makeQuery(id+"F18.imprint","IMPRINT",FACE,{"disambiguationData":[TD([[makeQuery(id+"F18.imprint","IMPRINT",EDGE,{"derivedFrom":subQ0}),1.0]])]});}
            var Q6;
            {var subQ0=sQuery(id+"F18.wireOp",EDGE,"E132");Q6=makeQuery(id+"F18.imprint","IMPRINT",FACE,{"disambiguationData":[TD([[makeQuery(id+"F18.imprint","IMPRINT",EDGE,{"derivedFrom":subQ0}),-1.0]])]});}
            var Q7;
            {var subQ0=sQuery(id+"F18.wireOp",EDGE,"E134");Q7=makeQuery(id+"F18.imprint","IMPRINT",FACE,{"disambiguationData":[TD([[makeQuery(id+"F18.imprint","IMPRINT",EDGE,{"derivedFrom":subQ0}),-1.0]])]});}
            var Q8;
            {var subQ0=sQuery(id+"F18.wireOp",EDGE,"E142.MirrorCS");Q8=makeQuery(id+"F18.imprint","IMPRINT",FACE,{"disambiguationData":[TD([[makeQuery(id+"F18.imprint","IMPRINT",EDGE,{"derivedFrom":subQ0}),1.0]])]});}
            var Q9;
            {var subQ0=sQuery(id+"F18.wireOp",EDGE,"E143.MirrorCS");Q9=makeQuery(id+"F18.imprint","IMPRINT",FACE,{"disambiguationData":[TD([[makeQuery(id+"F18.imprint","IMPRINT",EDGE,{"derivedFrom":subQ0}),1.0]])]});}
            var Q10;
            Q10=makeQuery(id+"F18.imprint","IMPRINT",FACE,{"disambiguationData":[TD([[makeQuery(id+"F18.imprint","IMPRINT",EDGE,{"derivedFrom":sQuery(id+"F18.wireOp",EDGE,"E138.0")}),1.0]])]});
            var Q11;
            Q11=makeQuery(id+"F16.opExtrude","SWEPT_FACE",FACE,{"disambiguationData":[OSD([sQuery(id+"F15.wireOp",EDGE,"E117")])]});
            extrude(context, id + "F19", {"entities" : qUnion([Q0, Q1, Q2, Q3, Q4, Q5, Q6, Q7, Q8, Q9, Q10]), "operationType" : NewBodyOperationType.REMOVE, "endBound" : BoundingType.UP_TO_SURFACE, "oppositeDirection" : true, "depth" : 25 * mm, "endBoundEntityFace" : qUnion([Q11]), "offsetDistance" : 25 * mm});
        }
        {
            var Q0;
            Q0=makeQuery(id+"F1.opExtrude","SWEPT_BODY",BODY,{"disambiguationData":[OSD([sQuery(id+"F0.wireOp",EDGE,"E0"),sQuery(id+"F0.wireOp",EDGE,"E1"),sQuery(id+"F0.wireOp",EDGE,"E2"),sQuery(id+"F0.wireOp",EDGE,"E3"),sQuery(id+"F0.wireOp",EDGE,"E5"),sQuery(id+"F0.wireOp",EDGE,"E6"),sQuery(id+"F0.wireOp",EDGE,"E7")])]});
            var Q1;
            Q1=qCreatedBy(id+"F12.planeOp",FACE);
            mirror(context, id + "F20", {"entities" : qUnion([Q0]), "mirrorPlane" : qUnion([Q1])});
        }
        {
            var Q0;
            Q0=makeQuery(id+"F1.opExtrude","CAP_FACE",FACE,{"disambiguationData":[OSD([sQuery(id+"F0.wireOp",EDGE,"E0"),sQuery(id+"F0.wireOp",EDGE,"E1"),sQuery(id+"F0.wireOp",EDGE,"E2"),sQuery(id+"F0.wireOp",EDGE,"E3"),sQuery(id+"F0.wireOp",EDGE,"E5"),sQuery(id+"F0.wireOp",EDGE,"E6"),sQuery(id+"F0.wireOp",EDGE,"E7")])],"isStart":false});
            var sketch = newSketch(context, id + "F21", { "sketchPlane" : qUnion([Q0])});
            skLineSegment(sketch, "E168", {"start": v(-411.35, 332.32) * mm, "end": v(-427.92, 292.32) * mm});
            skLineSegment(sketch, "E169", {"start": v(-427.92, 292.32) * mm, "end": v(-121.08, 292.32) * mm});
            skLineSegment(sketch, "E170", {"start": v(-121.08, 292.32) * mm, "end": v(-137.65, 332.32) * mm});
            skLineSegment(sketch, "E171", {"start": v(-137.65, 332.32) * mm, "end": v(-411.35, 332.32) * mm});
            skLineSegment(sketch, "E172", {"start": v(-507.02, 101.35) * mm, "end": v(-523.59, 61.35) * mm});
            skLineSegment(sketch, "E173", {"start": v(-523.59, 61.35) * mm, "end": v(-25.41, 61.35) * mm});
            skLineSegment(sketch, "E174", {"start": v(-25.41, 61.35) * mm, "end": v(-41.98, 101.35) * mm});
            skLineSegment(sketch, "E175", {"start": v(-41.98, 101.35) * mm, "end": v(-507.02, 101.35) * mm});
            skLineSegment(sketch, "E176", {"start": v(-419.63, 312.32) * mm, "end": v(-129.37, 312.32) * mm, "construction": true});
            skCircle(sketch, "E177", {"center": v(-388.4, 312.32) * mm, "radius": 6.25 * mm});
            skCircle(sketch, "E178", {"center": v(-274.5, 312.32) * mm, "radius": 6.25 * mm});
            skCircle(sketch, "E179", {"center": v(-160.6, 312.32) * mm, "radius": 6.25 * mm});
            skLineSegment(sketch, "E180", {"start": v(-515.3, 81.35) * mm, "end": v(-33.7, 81.35) * mm, "construction": true});
            skCircle(sketch, "E181", {"center": v(-484.08, 81.35) * mm, "radius": 6.25 * mm});
            skCircle(sketch, "E182", {"center": v(-274.5, 81.35) * mm, "radius": 6.25 * mm});
            skCircle(sketch, "E183", {"center": v(-64.92, 81.35) * mm, "radius": 6.25 * mm});
            skLineSegment(sketch, "E184", {"start": v(-358.92, 458.89) * mm, "end": v(-375.49, 418.89) * mm});
            skLineSegment(sketch, "E185", {"start": v(-375.49, 418.89) * mm, "end": v(-173.5, 418.89) * mm});
            skLineSegment(sketch, "E186", {"start": v(-173.5, 418.89) * mm, "end": v(-190.08, 458.89) * mm});
            skLineSegment(sketch, "E187", {"start": v(-190.08, 458.89) * mm, "end": v(-358.92, 458.89) * mm});
            skLineSegment(sketch, "E188", {"start": v(-367.2, 438.89) * mm, "end": v(-181.8, 438.89) * mm, "construction": true});
            skCircle(sketch, "E189", {"center": v(-213.02, 438.89) * mm, "radius": 6.25 * mm});
            skCircle(sketch, "E190", {"center": v(-335.98, 438.89) * mm, "radius": 6.25 * mm});
            skSolve(sketch);
        }
        {
            var Q0;
            Q0=qSketchRegion(id+"F21",true);
            extrude(context, id + "F22", {"entities" : qUnion([Q0]), "depth" : 4 * mm, "offsetDistance" : 25 * mm});
        }
        {
            var Q0;
            Q0=makeQuery(id+"F22.opExtrude","SWEPT_EDGE",EDGE,{"disambiguationData":[OSD([sQuery(id+"F21.wireOp",EDGE,"E172"),sQuery(id+"F21.wireOp",EDGE,"E173")])]});
            var Q1;
            Q1=makeQuery(id+"F22.opExtrude","SWEPT_EDGE",EDGE,{"disambiguationData":[OSD([sQuery(id+"F21.wireOp",EDGE,"E172"),sQuery(id+"F21.wireOp",EDGE,"E175")])]});
            var Q2;
            Q2=makeQuery(id+"F22.opExtrude","SWEPT_EDGE",EDGE,{"disambiguationData":[OSD([sQuery(id+"F21.wireOp",EDGE,"E173"),sQuery(id+"F21.wireOp",EDGE,"E174")])]});
            var Q3;
            Q3=makeQuery(id+"F22.opExtrude","SWEPT_EDGE",EDGE,{"disambiguationData":[OSD([sQuery(id+"F21.wireOp",EDGE,"E174"),sQuery(id+"F21.wireOp",EDGE,"E175")])]});
            var Q4;
            Q4=makeQuery(id+"F22.opExtrude","SWEPT_EDGE",EDGE,{"disambiguationData":[OSD([sQuery(id+"F21.wireOp",EDGE,"E170"),sQuery(id+"F21.wireOp",EDGE,"E171")])]});
            var Q5;
            Q5=makeQuery(id+"F22.opExtrude","SWEPT_EDGE",EDGE,{"disambiguationData":[OSD([sQuery(id+"F21.wireOp",EDGE,"E169"),sQuery(id+"F21.wireOp",EDGE,"E170")])]});
            var Q6;
            Q6=makeQuery(id+"F22.opExtrude","SWEPT_EDGE",EDGE,{"disambiguationData":[OSD([sQuery(id+"F21.wireOp",EDGE,"E168"),sQuery(id+"F21.wireOp",EDGE,"E169")])]});
            var Q7;
            Q7=makeQuery(id+"F22.opExtrude","SWEPT_EDGE",EDGE,{"disambiguationData":[OSD([sQuery(id+"F21.wireOp",EDGE,"E168"),sQuery(id+"F21.wireOp",EDGE,"E171")])]});
            var Q8;
            Q8=makeQuery(id+"F22.opExtrude","SWEPT_EDGE",EDGE,{"disambiguationData":[OSD([sQuery(id+"F21.wireOp",EDGE,"E184"),sQuery(id+"F21.wireOp",EDGE,"E187")])]});
            var Q9;
            Q9=makeQuery(id+"F22.opExtrude","SWEPT_EDGE",EDGE,{"disambiguationData":[OSD([sQuery(id+"F21.wireOp",EDGE,"E184"),sQuery(id+"F21.wireOp",EDGE,"E185")])]});
            var Q10;
            Q10=makeQuery(id+"F22.opExtrude","SWEPT_EDGE",EDGE,{"disambiguationData":[OSD([sQuery(id+"F21.wireOp",EDGE,"E186"),sQuery(id+"F21.wireOp",EDGE,"E187")])]});
            var Q11;
            Q11=makeQuery(id+"F22.opExtrude","SWEPT_EDGE",EDGE,{"disambiguationData":[OSD([sQuery(id+"F21.wireOp",EDGE,"E185"),sQuery(id+"F21.wireOp",EDGE,"E186")])]});
            fillet(context, id + "F23", {"entities" : qUnion([Q0, Q1, Q2, Q3, Q4, Q5, Q6, Q7, Q8, Q9, Q10, Q11]), "radius" : 10 * mm, "tangentPropagation" : true, "allowEdgeOverflow" : false});
        }
        {
            var Q0;
            Q0=makeQuery(id+"F22.opExtrude","SWEPT_BODY",BODY,{"disambiguationData":[OSD([sQuery(id+"F21.wireOp",EDGE,"E172"),sQuery(id+"F21.wireOp",EDGE,"E173"),sQuery(id+"F21.wireOp",EDGE,"E174"),sQuery(id+"F21.wireOp",EDGE,"E175"),sQuery(id+"F21.wireOp",EDGE,"E181"),sQuery(id+"F21.wireOp",EDGE,"E182"),sQuery(id+"F21.wireOp",EDGE,"E183")])]});
            var Q1;
            Q1=makeQuery(id+"F22.opExtrude","SWEPT_BODY",BODY,{"disambiguationData":[OSD([sQuery(id+"F21.wireOp",EDGE,"E168"),sQuery(id+"F21.wireOp",EDGE,"E169"),sQuery(id+"F21.wireOp",EDGE,"E170"),sQuery(id+"F21.wireOp",EDGE,"E171"),sQuery(id+"F21.wireOp",EDGE,"E177"),sQuery(id+"F21.wireOp",EDGE,"E178"),sQuery(id+"F21.wireOp",EDGE,"E179")])]});
            var Q2;
            Q2=makeQuery(id+"F22.opExtrude","SWEPT_BODY",BODY,{"disambiguationData":[OSD([sQuery(id+"F21.wireOp",EDGE,"E184"),sQuery(id+"F21.wireOp",EDGE,"E185"),sQuery(id+"F21.wireOp",EDGE,"E186"),sQuery(id+"F21.wireOp",EDGE,"E187"),sQuery(id+"F21.wireOp",EDGE,"E189"),sQuery(id+"F21.wireOp",EDGE,"E190")])]});
            var Q3;
            Q3=qCreatedBy(id+"F13.planeOp",FACE);
            mirror(context, id + "F24", {"entities" : qUnion([Q0, Q1, Q2]), "mirrorPlane" : qUnion([Q3])});
        }
        {
            var Q0;
            Q0=makeQuery(id+"F8.opExtrude","CAP_FACE",FACE,{"disambiguationData":[OSD([sQuery(id+"F7.wireOp",EDGE,"E57"),sQuery(id+"F7.wireOp",EDGE,"E58"),sQuery(id+"F7.wireOp",EDGE,"E59"),sQuery(id+"F7.wireOp",EDGE,"E60"),sQuery(id+"F7.wireOp",EDGE,"E63"),sQuery(id+"F7.wireOp",EDGE,"E65"),sQuery(id+"F7.wireOp",EDGE,"E66"),sQuery(id+"F7.wireOp",EDGE,"E67"),sQuery(id+"F7.wireOp",EDGE,"E68"),sQuery(id+"F7.wireOp",EDGE,"E69")])],"isStart":true});
            cPlane(context, id + "F25", {"entities" : qUnion([Q0]), "cplaneType" : CPlaneType.OFFSET, "offset" : 300 * mm, "width" : 150 * mm, "height" : 150 * mm});
        }
        {
            var Q0;
            Q0=makeQuery(id+"F1.opExtrude","SWEPT_BODY",BODY,{"disambiguationData":[OSD([sQuery(id+"F0.wireOp",EDGE,"E0"),sQuery(id+"F0.wireOp",EDGE,"E1"),sQuery(id+"F0.wireOp",EDGE,"E2"),sQuery(id+"F0.wireOp",EDGE,"E3"),sQuery(id+"F0.wireOp",EDGE,"E5"),sQuery(id+"F0.wireOp",EDGE,"E6"),sQuery(id+"F0.wireOp",EDGE,"E7")])]});
            var Q1;
            Q1=makeQuery(id+"F20.opPattern","COPY",BODY,{"derivedFrom":makeQuery(id+"F1.opExtrude","SWEPT_BODY",BODY,{"disambiguationData":[OSD([sQuery(id+"F0.wireOp",EDGE,"E0"),sQuery(id+"F0.wireOp",EDGE,"E1"),sQuery(id+"F0.wireOp",EDGE,"E2"),sQuery(id+"F0.wireOp",EDGE,"E3"),sQuery(id+"F0.wireOp",EDGE,"E5"),sQuery(id+"F0.wireOp",EDGE,"E6"),sQuery(id+"F0.wireOp",EDGE,"E7")])]}),"instanceName":"1"});
            var Q2;
            Q2=makeQuery(id+"F22.opExtrude","SWEPT_BODY",BODY,{"disambiguationData":[OSD([sQuery(id+"F21.wireOp",EDGE,"E172"),sQuery(id+"F21.wireOp",EDGE,"E173"),sQuery(id+"F21.wireOp",EDGE,"E174"),sQuery(id+"F21.wireOp",EDGE,"E175"),sQuery(id+"F21.wireOp",EDGE,"E181"),sQuery(id+"F21.wireOp",EDGE,"E182"),sQuery(id+"F21.wireOp",EDGE,"E183")])]});
            var Q3;
            Q3=makeQuery(id+"F22.opExtrude","SWEPT_BODY",BODY,{"disambiguationData":[OSD([sQuery(id+"F21.wireOp",EDGE,"E168"),sQuery(id+"F21.wireOp",EDGE,"E169"),sQuery(id+"F21.wireOp",EDGE,"E170"),sQuery(id+"F21.wireOp",EDGE,"E171"),sQuery(id+"F21.wireOp",EDGE,"E177"),sQuery(id+"F21.wireOp",EDGE,"E178"),sQuery(id+"F21.wireOp",EDGE,"E179")])]});
            var Q4;
            Q4=makeQuery(id+"F22.opExtrude","SWEPT_BODY",BODY,{"disambiguationData":[OSD([sQuery(id+"F21.wireOp",EDGE,"E184"),sQuery(id+"F21.wireOp",EDGE,"E185"),sQuery(id+"F21.wireOp",EDGE,"E186"),sQuery(id+"F21.wireOp",EDGE,"E187"),sQuery(id+"F21.wireOp",EDGE,"E189"),sQuery(id+"F21.wireOp",EDGE,"E190")])]});
            var Q5;
            Q5=makeQuery(id+"F24.opPattern","COPY",BODY,{"derivedFrom":makeQuery(id+"F22.opExtrude","SWEPT_BODY",BODY,{"disambiguationData":[OSD([sQuery(id+"F21.wireOp",EDGE,"E168"),sQuery(id+"F21.wireOp",EDGE,"E169"),sQuery(id+"F21.wireOp",EDGE,"E170"),sQuery(id+"F21.wireOp",EDGE,"E171"),sQuery(id+"F21.wireOp",EDGE,"E177"),sQuery(id+"F21.wireOp",EDGE,"E178"),sQuery(id+"F21.wireOp",EDGE,"E179")])]}),"instanceName":"1"});
            var Q6;
            Q6=makeQuery(id+"F24.opPattern","COPY",BODY,{"derivedFrom":makeQuery(id+"F22.opExtrude","SWEPT_BODY",BODY,{"disambiguationData":[OSD([sQuery(id+"F21.wireOp",EDGE,"E184"),sQuery(id+"F21.wireOp",EDGE,"E185"),sQuery(id+"F21.wireOp",EDGE,"E186"),sQuery(id+"F21.wireOp",EDGE,"E187"),sQuery(id+"F21.wireOp",EDGE,"E189"),sQuery(id+"F21.wireOp",EDGE,"E190")])]}),"instanceName":"1"});
            var Q7;
            Q7=makeQuery(id+"F24.opPattern","COPY",BODY,{"derivedFrom":makeQuery(id+"F22.opExtrude","SWEPT_BODY",BODY,{"disambiguationData":[OSD([sQuery(id+"F21.wireOp",EDGE,"E172"),sQuery(id+"F21.wireOp",EDGE,"E173"),sQuery(id+"F21.wireOp",EDGE,"E174"),sQuery(id+"F21.wireOp",EDGE,"E175"),sQuery(id+"F21.wireOp",EDGE,"E181"),sQuery(id+"F21.wireOp",EDGE,"E182"),sQuery(id+"F21.wireOp",EDGE,"E183")])]}),"instanceName":"1"});
            var Q8;
            Q8=makeQuery(id+"F8.opExtrude","SWEPT_BODY",BODY,{"disambiguationData":[OSD([sQuery(id+"F7.wireOp",EDGE,"E57"),sQuery(id+"F7.wireOp",EDGE,"E58"),sQuery(id+"F7.wireOp",EDGE,"E59"),sQuery(id+"F7.wireOp",EDGE,"E60"),sQuery(id+"F7.wireOp",EDGE,"E63"),sQuery(id+"F7.wireOp",EDGE,"E65"),sQuery(id+"F7.wireOp",EDGE,"E66"),sQuery(id+"F7.wireOp",EDGE,"E67"),sQuery(id+"F7.wireOp",EDGE,"E68"),sQuery(id+"F7.wireOp",EDGE,"E69")])]});
            var Q9;
            Q9=makeQuery(id+"F16.opExtrude","SWEPT_BODY",BODY,{"disambiguationData":[OSD([sQuery(id+"F15.wireOp",EDGE,"E116"),sQuery(id+"F15.wireOp",EDGE,"E117"),sQuery(id+"F15.wireOp",EDGE,"E118"),sQuery(id+"F15.wireOp",EDGE,"E119"),sQuery(id+"F15.wireOp",EDGE,"E121"),sQuery(id+"F15.wireOp",EDGE,"E122"),sQuery(id+"F15.wireOp",EDGE,"E123"),sQuery(id+"F15.wireOp",EDGE,"E124"),sQuery(id+"F15.wireOp",EDGE,"E125"),sQuery(id+"F15.wireOp",EDGE,"E126"),sQuery(id+"F15.wireOp",EDGE,"E127"),sQuery(id+"F15.wireOp",EDGE,"E128")])]});
            var Q10;
            Q10=makeQuery(id+"FNHB49UKIk5wtmY_5.opExtrude","SWEPT_BODY",BODY,{"disambiguationData":[OSD([sQuery(id+"FfIjeSQml9yg72F_5.wireOp",EDGE,"UkjUz414-lFb8-aQT4-BZFm-E69EYXlYXt0V"),sQuery(id+"FfIjeSQml9yg72F_5.wireOp",EDGE,"sISkosFA-JdbD-0We7-Mf9U-FgGv5622x6BR"),sQuery(id+"FfIjeSQml9yg72F_5.wireOp",EDGE,"vEgnGYEY-utzF-OeVs-Nw7k-37XqNCZrhnXe"),sQuery(id+"FfIjeSQml9yg72F_5.wireOp",EDGE,"i90yqODP-gGDX-CLg9-7yaR-nyb6uMeF0iIx"),sQuery(id+"FfIjeSQml9yg72F_5.wireOp",EDGE,"DnHAWWsv-YZhk-M76l-A9QL-FzHdJCn6Qm1x"),sQuery(id+"FfIjeSQml9yg72F_5.wireOp",EDGE,"yluItiY8-Uhai-oYCZ-q9aJ-CL20OdbyFMZ6"),sQuery(id+"FfIjeSQml9yg72F_5.wireOp",EDGE,"K6IAHcUk-SDMV-bZ1v-Tbl0-PwxRQBWMNn03")])]});
            var Q11;
            Q11=qCreatedBy(id+"F25.planeOp",FACE);
            mirror(context, id + "F26", {"entities" : qUnion([Q0, Q1, Q2, Q3, Q4, Q5, Q6, Q7, Q8, Q9, Q10]), "mirrorPlane" : qUnion([Q11])});
        }
        {
            var Q0;
            {var subQ0=sQuery(id+"F0.wireOp",EDGE,"E3");Q0=makeQuery(id+"F6.boolean.opBoolean","SPLIT",FACE,{"disambiguationData":[TD([makeQuery(id+"F6.opExtrude","SWEPT_FACE",FACE,{"disambiguationData":[OSD([sQuery(id+"F5.wireOp",EDGE,"E46.MirrorCS")])]})])],"derivedFrom":makeQuery(id+"F1.opExtrude","SWEPT_FACE",FACE,{"disambiguationData":[OSD([subQ0])]})});}
            var sketch = newSketch(context, id + "F27", { "sketchPlane" : qUnion([Q0])});
            skLineSegment(sketch, "E191", {"start": v(-720, 130) * mm, "end": v(0, 130) * mm});
            skLineSegment(sketch, "E192", {"start": v(0, 130) * mm, "end": v(0, 170) * mm});
            skLineSegment(sketch, "E193", {"start": v(0, 170) * mm, "end": v(-720, 170) * mm});
            skLineSegment(sketch, "E194", {"start": v(-720, 170) * mm, "end": v(-720, 130) * mm});
            skLineSegment(sketch, "E195", {"start": v(-720, 150) * mm, "end": v(0, 150) * mm, "construction": true});
            skCircle(sketch, "E196", {"center": v(-690, 150) * mm, "radius": 6.25 * mm});
            skCircle(sketch, "E197", {"center": v(-30, 150) * mm, "radius": 6.25 * mm});
            skLineSegment(sketch, "E198", {"start": v(0, 320) * mm, "end": v(-720, 320) * mm});
            skLineSegment(sketch, "E199", {"start": v(-720, 320) * mm, "end": v(-720, 280) * mm});
            skLineSegment(sketch, "E200", {"start": v(-720, 280) * mm, "end": v(0, 280) * mm});
            skLineSegment(sketch, "E201", {"start": v(0, 280) * mm, "end": v(0, 320) * mm});
            skLineSegment(sketch, "E202", {"start": v(0, 300) * mm, "end": v(-720, 300) * mm, "construction": true});
            skCircle(sketch, "E203", {"center": v(-690, 300) * mm, "radius": 6.25 * mm});
            skCircle(sketch, "E204", {"center": v(-30, 300) * mm, "radius": 6.25 * mm});
            skSolve(sketch);
        }
        {
            var Q0;
            Q0=qSketchRegion(id+"F27",true);
            extrude(context, id + "F28", {"entities" : qUnion([Q0]), "depth" : 4 * mm, "offsetDistance" : 25 * mm});
        }
        {
            var Q0;
            Q0=makeQuery(id+"F28.opExtrude","SWEPT_EDGE",EDGE,{"disambiguationData":[OSD([sQuery(id+"F27.wireOp",EDGE,"E193"),sQuery(id+"F27.wireOp",EDGE,"E194")])]});
            var Q1;
            Q1=makeQuery(id+"F28.opExtrude","SWEPT_EDGE",EDGE,{"disambiguationData":[OSD([sQuery(id+"F27.wireOp",EDGE,"E191"),sQuery(id+"F27.wireOp",EDGE,"E194")])]});
            var Q2;
            Q2=makeQuery(id+"F28.opExtrude","SWEPT_EDGE",EDGE,{"disambiguationData":[OSD([sQuery(id+"F27.wireOp",EDGE,"E192"),sQuery(id+"F27.wireOp",EDGE,"E193")])]});
            var Q3;
            Q3=makeQuery(id+"F28.opExtrude","SWEPT_EDGE",EDGE,{"disambiguationData":[OSD([sQuery(id+"F27.wireOp",EDGE,"E191"),sQuery(id+"F27.wireOp",EDGE,"E192")])]});
            var Q4;
            Q4=makeQuery(id+"F28.opExtrude","SWEPT_EDGE",EDGE,{"disambiguationData":[OSD([sQuery(id+"F27.wireOp",EDGE,"E198"),sQuery(id+"F27.wireOp",EDGE,"E199")])]});
            var Q5;
            Q5=makeQuery(id+"F28.opExtrude","SWEPT_EDGE",EDGE,{"disambiguationData":[OSD([sQuery(id+"F27.wireOp",EDGE,"E199"),sQuery(id+"F27.wireOp",EDGE,"E200")])]});
            var Q6;
            Q6=makeQuery(id+"F28.opExtrude","SWEPT_EDGE",EDGE,{"disambiguationData":[OSD([sQuery(id+"F27.wireOp",EDGE,"E200"),sQuery(id+"F27.wireOp",EDGE,"E201")])]});
            var Q7;
            Q7=makeQuery(id+"F28.opExtrude","SWEPT_EDGE",EDGE,{"disambiguationData":[OSD([sQuery(id+"F27.wireOp",EDGE,"E198"),sQuery(id+"F27.wireOp",EDGE,"E201")])]});
            fillet(context, id + "F29", {"entities" : qUnion([Q0, Q1, Q2, Q3, Q4, Q5, Q6, Q7]), "radius" : 10 * mm, "tangentPropagation" : true, "allowEdgeOverflow" : false});
        }
        {
            var Q0;
            Q0=makeQuery(id+"F19.boolean.opBoolean","COPY",FACE,{"derivedFrom":makeQuery(id+"F19.opExtrude","SWEPT_FACE",FACE,{"disambiguationData":[OSD([sQuery(id+"F18.wireOp",EDGE,"E140"),sQuery(id+"F18.wireOp",EDGE,"E158.MirrorCS")])]})});
            var Q1;
            Q1=makeQuery(id+"F19.boolean.opBoolean","COPY",FACE,{"derivedFrom":makeQuery(id+"F19.opExtrude","SWEPT_FACE",FACE,{"disambiguationData":[OSD([sQuery(id+"F18.wireOp",EDGE,"E147.MirrorCS"),sQuery(id+"F18.wireOp",EDGE,"E166.MirrorCS")])]})});
            cPlane(context, id + "F30", {"entities" : qUnion([Q0, Q1]), "cplaneType" : CPlaneType.MID_PLANE, "offset" : 25 * mm, "width" : 150 * mm, "height" : 150 * mm});
        }
        {
            var Q0;
            Q0=makeQuery(id+"F28.opExtrude","SWEPT_BODY",BODY,{"disambiguationData":[OSD([sQuery(id+"F27.wireOp",EDGE,"E191"),sQuery(id+"F27.wireOp",EDGE,"E192"),sQuery(id+"F27.wireOp",EDGE,"E193"),sQuery(id+"F27.wireOp",EDGE,"E194"),sQuery(id+"F27.wireOp",EDGE,"E196"),sQuery(id+"F27.wireOp",EDGE,"E197")])]});
            var Q1;
            Q1=makeQuery(id+"F28.opExtrude","SWEPT_BODY",BODY,{"disambiguationData":[OSD([sQuery(id+"F27.wireOp",EDGE,"E198"),sQuery(id+"F27.wireOp",EDGE,"E199"),sQuery(id+"F27.wireOp",EDGE,"E200"),sQuery(id+"F27.wireOp",EDGE,"E201"),sQuery(id+"F27.wireOp",EDGE,"E203"),sQuery(id+"F27.wireOp",EDGE,"E204")])]});
            var Q2;
            Q2=qCreatedBy(id+"F30.planeOp",FACE);
            mirror(context, id + "F31", {"entities" : qUnion([Q0, Q1]), "mirrorPlane" : qUnion([Q2])});
        }
        {
            var Q0;
            Q0=qCreatedBy(id+"F25.planeOp",FACE);
            var sketch = newSketch(context, id + "F32", { "sketchPlane" : qUnion([Q0])});
            skCircle(sketch, "E205", {"center": v(-274.5, 920) * mm, "radius": 5.9 * mm});
            skSolve(sketch);
        }
        {
            var Q0;
            Q0=qSketchRegion(id+"F32",true);
            extrude(context, id + "F33", {"entities" : qUnion([Q0]), "endBound" : BoundingType.SYMMETRIC, "depth" : 750 * mm, "offsetDistance" : 25 * mm});
        }
        {
            var Q0;
            Q0=qCreatedBy(id+"F30.planeOp",FACE);
            var sketch = newSketch(context, id + "F34", { "sketchPlane" : qUnion([Q0])});
            skLineSegment(sketch, "E206", {"start": v(60, 926.25) * mm, "end": v(60, 940) * mm});
            skLineSegment(sketch, "E207", {"start": v(60, 940) * mm, "end": v(75, 940) * mm});
            skLineSegment(sketch, "E208", {"start": v(75, 940) * mm, "end": v(75, 950) * mm});
            skLineSegment(sketch, "E209", {"start": v(75, 950) * mm, "end": v(360, 950) * mm});
            skLineSegment(sketch, "E210", {"start": v(360, 950) * mm, "end": v(360, 926.25) * mm, "construction": true});
            skLineSegment(sketch, "E211", {"start": v(360, 926.25) * mm, "end": v(60, 926.25) * mm});
            skLineSegment(sketch, "E212", {"start": v(60, 926.25) * mm, "end": v(60, 920) * mm, "construction": true});
            skLineSegment(sketch, "E213", {"start": v(60, 920) * mm, "end": v(360, 920) * mm, "construction": true});
            skLineSegment(sketch, "E214", {"start": v(360, 920) * mm, "end": v(360, 926.25) * mm, "construction": true});
            skLineSegment(sketch, "E215.MirrorCS", {"start": v(660, 926.25) * mm, "end": v(660, 920) * mm, "construction": true});
            skLineSegment(sketch, "E216.MirrorCS", {"start": v(660, 926.25) * mm, "end": v(660, 940) * mm});
            skLineSegment(sketch, "E217.MirrorCS", {"start": v(645, 940) * mm, "end": v(645, 950) * mm});
            skLineSegment(sketch, "E218.MirrorCS", {"start": v(660, 940) * mm, "end": v(645, 940) * mm});
            skLineSegment(sketch, "E219.MirrorCS", {"start": v(645, 950) * mm, "end": v(360, 950) * mm});
            skLineSegment(sketch, "E220.MirrorCS", {"start": v(660, 920) * mm, "end": v(360, 920) * mm, "construction": true});
            skLineSegment(sketch, "E221.MirrorCS", {"start": v(360, 926.25) * mm, "end": v(660, 926.25) * mm});
            skSolve(sketch);
        }
        {
            var Q0;
            Q0 = qSketchRegion(id + "F34", true);
            var Q1;
            Q1=makeQuery(id+"F33.opExtrude","SWEPT_FACE",FACE,{"disambiguationData":[OSD([sQuery(id+"F32.wireOp",EDGE,"E205")])]});
            revolve(context, id + "F35", {"surfaceOperationType" : NewSurfaceOperationType.NEW, "entities" : qUnion([Q0]), "axis" : qUnion([Q1]), "revolveType" : RevolveType.FULL});
        }
        {
            var Q0;
            Q0=makeQuery(id+"F33.opExtrude","CAP_EDGE",EDGE,{"disambiguationData":[OSD([sQuery(id+"F32.wireOp",EDGE,"E205")])],"isStart":false});
            var Q1;
            Q1=makeQuery(id+"F33.opExtrude","CAP_EDGE",EDGE,{"disambiguationData":[OSD([sQuery(id+"F32.wireOp",EDGE,"E205")])],"isStart":true});
            chamfer(context, id + "F36", {"entities" : qUnion([Q0, Q1]), "width" : 2 * mm, "tangentPropagation" : true});
        }
        {
            var Q0;
            Q0=makeQuery(id+"F35.opRevolve","SWEPT_FACE",FACE,{"disambiguationData":[OSD([sQuery(id+"F34.wireOp",EDGE,"E209"),sQuery(id+"F34.wireOp",EDGE,"E219.MirrorCS")])]});
            cPlane(context, id + "F37", {"entities" : qUnion([Q0]), "cplaneType" : CPlaneType.LINE_ANGLE, "offset" : 25 * mm, "angle" : 0 * degree, "width" : 150 * mm, "height" : 150 * mm});
        }
        {
            var Q0;
            Q0=makeQuery(id+"F35.opRevolve","SWEPT_EDGE",EDGE,{"disambiguationData":[OSD([sQuery(id+"F34.wireOp",EDGE,"E217.MirrorCS"),sQuery(id+"F34.wireOp",EDGE,"E219.MirrorCS")])]});
            var Q1;
            Q1=makeQuery(id+"F35.opRevolve","SWEPT_EDGE",EDGE,{"disambiguationData":[OSD([sQuery(id+"F34.wireOp",EDGE,"E208"),sQuery(id+"F34.wireOp",EDGE,"E209")])]});
            chamfer(context, id + "F38", {"entities" : qUnion([Q0, Q1]), "width" : 2.5 * mm, "tangentPropagation" : true});
        }
    });
